SOLIDWORKS PART (.sldprt)
format: sldprt  version: not decoded by parser v0  size: 196,096 bytes
history: native  units: mm
features: sketch x8, extrude x8, plane x3, material x1 (+13 scaffold rows collapsed)
feature tree (33):
  scaffold x13  (default folders/planes/origin — collapsed)
  material  "材质 <未指定>"
  plane  "前视基准面"
  plane  "上视基准面"
  plane  "右视基准面"
  sketch  "草图1"  dims[D4=~4.035653mm D1=80.0mm D2=4.0mm D3=10.0mm]
  extrude  "凸台-拉伸1"  Depth=1mm
  sketch  "草图2"
  extrude  "凸台-拉伸2"  Depth=1mm
  sketch  "草图3"  dims[D4=~6.875925mm D1=4.0mm D2=80.0mm D3=10.0mm]
  extrude  "凸台-拉伸3"  Depth=1mm
  sketch  "草图4"  dims[D4=~3.751705mm D1=4.0mm D2=10.0mm D3=80.0mm]
  extrude  "凸台-拉伸5"  Depth=1mm
  sketch  "草图5"  dims[D1=4.0mm]
  extrude  "凸台-拉伸6"  Depth=1mm
  sketch  "草图6"
  extrude  "凸台-拉伸7"  Depth=1mm
  sketch  "草图7"
  extrude  "凸台-拉伸8"  Depth=1mm
  sketch  "草图8"  dims[D1=0.0mm D2=1.5mm D3=1.5mm D4=2.0mm D5=0.0mm D6=1.5mm D7=1.5mm D8=2.0mm]
  extrude  "凸台-拉伸9"  Depth=1mm
decode coverage: 13 of 16 modeling features carry decoded parameters
note: ~ marks probable driven/reference dimensions
note: suppression state not decoded; provenance and decode notes live in map.json
